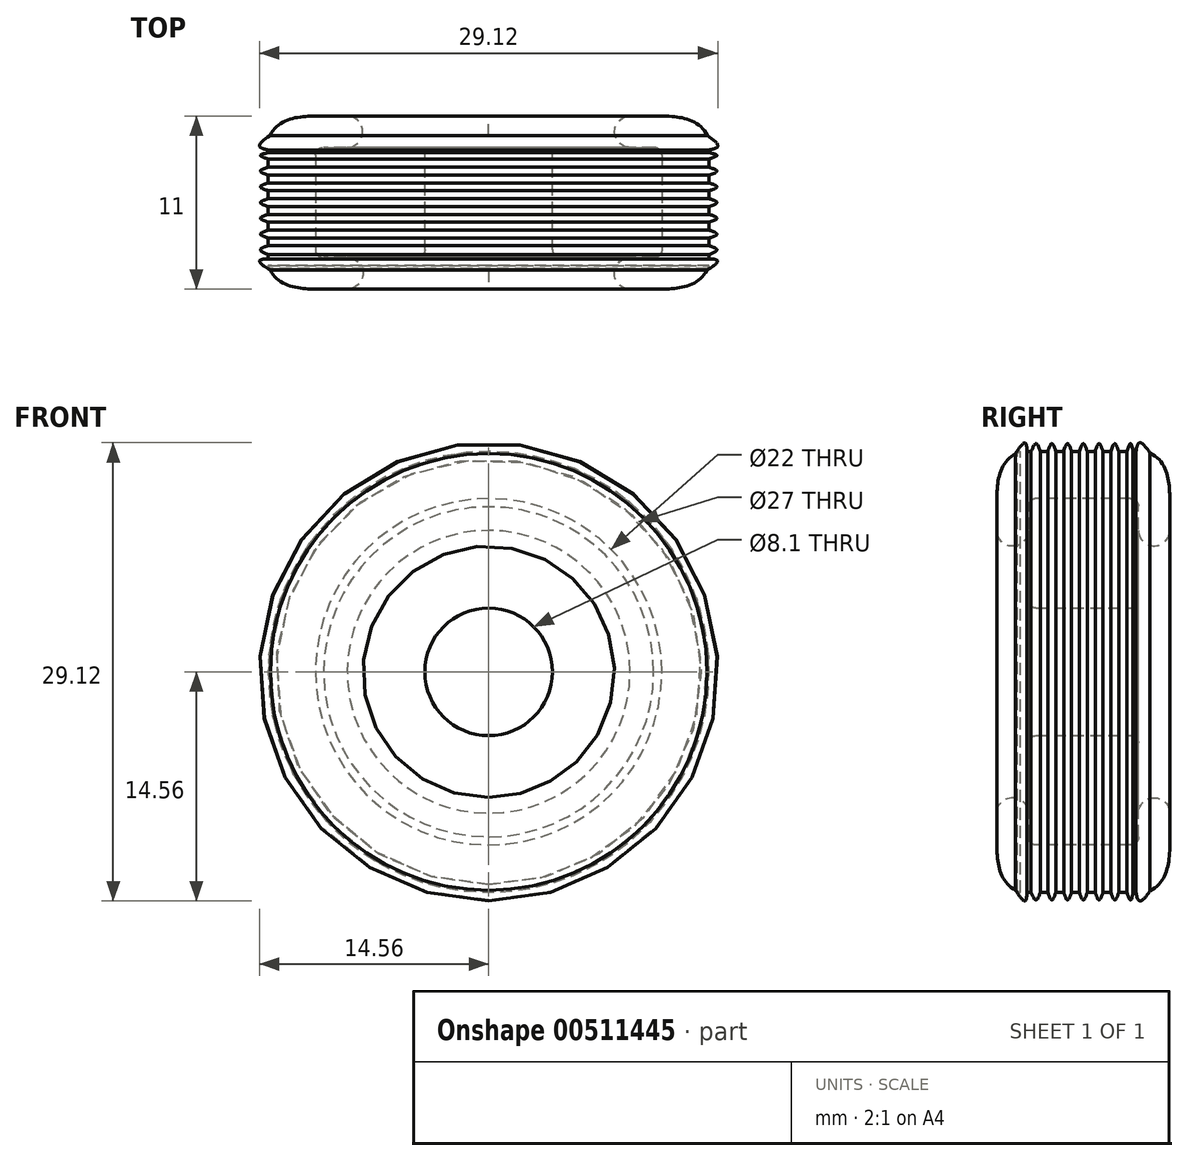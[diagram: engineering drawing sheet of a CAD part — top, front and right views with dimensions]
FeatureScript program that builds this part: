
annotation { "Feature Type Name" : "Feature", "Feature Type Description" : "" }
export const myFeature = defineFeature(function(context is Context, id is Id, definition is map)
    precondition{}
    {
        {
            var Q0;
            Q0=qCreatedBy(makeId("Front.planeOp"),FACE);
            var sketch = newSketch(context, id + "F0", { "sketchPlane" : qUnion([Q0])});
            skCircle(sketch, "E0", {"center": v(0, 0) * mm, "radius": 11 * mm});
            skCircle(sketch, "E1", {"center": v(0, 0) * mm, "radius": 4.05 * mm});
            skSolve(sketch);
        }
        {
            var Q0;
            Q0=makeQuery(id+"F0.imprint","IMPRINT",FACE,{"disambiguationData":[TD([[makeQuery(id+"F0.imprint","IMPRINT",EDGE,{"derivedFrom":sQuery(id+"F0.wireOp",EDGE,"E0")}),1.0]])]});
            extrude(context, id + "F1", {"entities" : qUnion([Q0]), "endBound" : BoundingType.SYMMETRIC, "depth" : 7 * mm, "offsetDistance" : 25 * mm});
        }
        {
            var Q0;
            Q0=makeQuery(id+"F1.opExtrude","CAP_EDGE",EDGE,{"disambiguationData":[OSD([sQuery(id+"F0.wireOp",EDGE,"E1")])],"isStart":true});
            var Q1;
            Q1=makeQuery(id+"F1.opExtrude","CAP_EDGE",EDGE,{"disambiguationData":[OSD([sQuery(id+"F0.wireOp",EDGE,"E1")])],"isStart":false});
            var Q2;
            Q2=makeQuery(id+"F1.opExtrude","CAP_EDGE",EDGE,{"disambiguationData":[OSD([sQuery(id+"F0.wireOp",EDGE,"E0")])],"isStart":true});
            var Q3;
            Q3=makeQuery(id+"F1.opExtrude","CAP_EDGE",EDGE,{"disambiguationData":[OSD([sQuery(id+"F0.wireOp",EDGE,"E0")])],"isStart":false});
            fillet(context, id + "F2", {"entities" : qUnion([Q0, Q1, Q2, Q3]), "tangentPropagation" : true, "radius" : .5 * mm, "defaultsChanged" : true, "vertexSettings" : [], "allowEdgeOverflow" : false});
        }
        {
            var Q0;
            Q0=qCreatedBy(makeId("Top.planeOp"),FACE);
            var sketch = newSketch(context, id + "F3", { "sketchPlane" : qUnion([Q0])});
            skLineSegment(sketch, "E2", {"start": v(0, 0) * mm, "end": v(11, 0) * mm, "construction": true});
            skLineSegment(sketch, "E3", {"start": v(11, -3) * mm, "end": v(11, 3) * mm});
            skArc(sketch, "E4", {"start": v(11, -3) * mm, "mid": v(10.85, -3.36) * mm, "end": v(10.48, -3.5) * mm});
            skLineSegment(sketch, "E5", {"start": v(10.48, -3.5) * mm, "end": v(8.98, -3.5) * mm});
            skArc(sketch, "E6.MirrorCS", {"start": v(11, 3) * mm, "mid": v(10.85, 3.36) * mm, "end": v(10.48, 3.5) * mm});
            skLineSegment(sketch, "E7.MirrorCS", {"start": v(10.48, 3.5) * mm, "end": v(8.98, 3.5) * mm});
            skLineSegment(sketch, "E8.0", {"start": v(10.46, 5.5) * mm, "end": v(9, 5.5) * mm});
            skLineSegment(sketch, "E8.1", {"start": v(10.46, -5.5) * mm, "end": v(8.98, -5.5) * mm});
            skArc(sketch, "E8.2", {"start": v(13, -3) * mm, "mid": v(12.25, -4.78) * mm, "end": v(10.46, -5.5) * mm, "construction": true});
            skLineSegment(sketch, "E8.3", {"start": v(13, -3) * mm, "end": v(13, 3) * mm, "construction": true});
            skArc(sketch, "E8.4", {"start": v(13, 3) * mm, "mid": v(12.25, 4.78) * mm, "end": v(10.46, 5.5) * mm, "construction": true});
            skArc(sketch, "E9", {"start": v(8.98, -5.5) * mm, "mid": v(7.98, -4.5) * mm, "end": v(8.98, -3.5) * mm});
            skLineSegment(sketch, "E10", {"start": v(13, 0) * mm, "end": v(14, 0) * mm, "construction": true});
            skLineSegment(sketch, "E11", {"start": v(14, -4) * mm, "end": v(14, 4) * mm});
            skFitSpline(sketch, "E12", {"points": [v(14, -4) * mm, v(10.46, -5.5) * mm], "startDerivative": vector(-1.61, -4.5) * mm, "endDerivative": vector(-4.23, 0) * mm});
            skLineSegment(sketch, "E13", {"start": v(10.46, -5.5) * mm, "end": v(16.46, -5.5) * mm, "construction": true});
            skFitSpline(sketch, "E14.MirrorCS", {"points": [v(14, 4) * mm, v(10.46, 5.5) * mm], "startDerivative": vector(-1.61, 4.5) * mm, "endDerivative": vector(-4.23, 0) * mm});
            skLineSegment(sketch, "E15", {"start": v(0, -3) * mm, "end": v(0, 3) * mm, "construction": true});
            skLineSegment(sketch, "E16", {"start": v(13.92, -4.2) * mm, "end": v(14, -4) * mm});
            skArc(sketch, "E17", {"start": v(9, 5.5) * mm, "mid": v(8, 4.5) * mm, "end": v(8.98, 3.5) * mm});
            skLineSegment(sketch, "E18", {"start": v(14, 4) * mm, "end": v(14.5, 4) * mm, "construction": true});
            skLineSegment(sketch, "E19", {"start": v(14.5, 4) * mm, "end": v(14.5, 3) * mm, "construction": true});
            skLineSegment(sketch, "E20", {"start": v(14.5, 3) * mm, "end": v(14.5, 2) * mm, "construction": true});
            skLineSegment(sketch, "E21", {"start": v(14.5, 2) * mm, "end": v(14.5, 1) * mm, "construction": true});
            skLineSegment(sketch, "E22", {"start": v(14.5, 1) * mm, "end": v(14.5, 0) * mm, "construction": true});
            skLineSegment(sketch, "E23", {"start": v(14.5, 0) * mm, "end": v(14.5, -1) * mm, "construction": true});
            skLineSegment(sketch, "E24", {"start": v(14.5, -1) * mm, "end": v(14.5, -2) * mm, "construction": true});
            skLineSegment(sketch, "E25", {"start": v(14.5, -2) * mm, "end": v(14.5, -3) * mm, "construction": true});
            skLineSegment(sketch, "E26", {"start": v(14.5, -3) * mm, "end": v(14.5, -4) * mm, "construction": true});
            skLineSegment(sketch, "E27", {"start": v(14, 4) * mm, "end": v(13.5, 4) * mm, "construction": true});
            skLineSegment(sketch, "E28", {"start": v(13.5, 4) * mm, "end": v(13.5, 2.5) * mm, "construction": true});
            skLineSegment(sketch, "E29", {"start": v(13.5, 2.5) * mm, "end": v(13.5, 1.5) * mm, "construction": true});
            skLineSegment(sketch, "E30", {"start": v(13.5, 1.5) * mm, "end": v(13.5, 0.5) * mm, "construction": true});
            skLineSegment(sketch, "E31", {"start": v(13.5, 0.5) * mm, "end": v(13.5, -0.5) * mm, "construction": true});
            skLineSegment(sketch, "E32", {"start": v(13.5, -0.5) * mm, "end": v(13.5, -1.5) * mm, "construction": true});
            skLineSegment(sketch, "E33", {"start": v(13.5, -1.5) * mm, "end": v(13.5, -2.5) * mm, "construction": true});
            skLineSegment(sketch, "E34", {"start": v(13.5, -2.5) * mm, "end": v(13.5, -3.53) * mm, "construction": true});
            skLineSegment(sketch, "E35", {"start": v(13.5, -3.53) * mm, "end": v(13.5, -4.09) * mm, "construction": true});
            skLineSegment(sketch, "E36", {"start": v(13.5, 4) * mm, "end": v(13.5, 0) * mm});
            skLineSegment(sketch, "E37", {"start": v(13.5, 0) * mm, "end": v(13.5, -4) * mm, "construction": true});
            skLineSegment(sketch, "E38", {"start": v(13.5, 2.5) * mm, "end": v(13.5, 3.5) * mm, "construction": true});
            skLineSegment(sketch, "E39", {"start": v(13.5, -3.53) * mm, "end": v(13.5, -4.53) * mm, "construction": true});
            skLineSegment(sketch, "E40", {"start": v(13.5, 4) * mm, "end": v(13.5, 4.5) * mm, "construction": true});
            skFitSpline(sketch, "E41", {"points": [v(13.5, 4.5) * mm, v(14.5, 3.5) * mm, v(13.5, 3.25) * mm, v(14.5, 3) * mm, v(13.5, 2.5) * mm, v(14.5, 2) * mm, v(13.5, 1.5) * mm, v(14.5, 1) * mm, v(13.5, 0.5) * mm, v(14.5, 0) * mm, v(13.5, -0.5) * mm, v(14.5, -1) * mm, v(13.5, -1.5) * mm, v(14.5, -2) * mm, v(13.5, -2.5) * mm, v(14.5, -3) * mm, v(13.5, -3.53) * mm, v(14.5, -3.65) * mm, v(13.5, -4.53) * mm], "startDerivative": vector(30.04, -19.27) * mm, "endDerivative": vector(-30.46, -18.6) * mm});
            skSolve(sketch);
        }
        {
            var Q0;
            Q0=qSketchRegion(id+"F3",true);
            var Q1;
            Q1=sQuery(id+"F3.wireOp",EDGE,"E15");
            revolve(context, id + "F4", {"surfaceOperationType" : NewSurfaceOperationType.NEW, "entities" : qUnion([Q0]), "axis" : qUnion([Q1]), "revolveType" : RevolveType.FULL});
        }
    });
